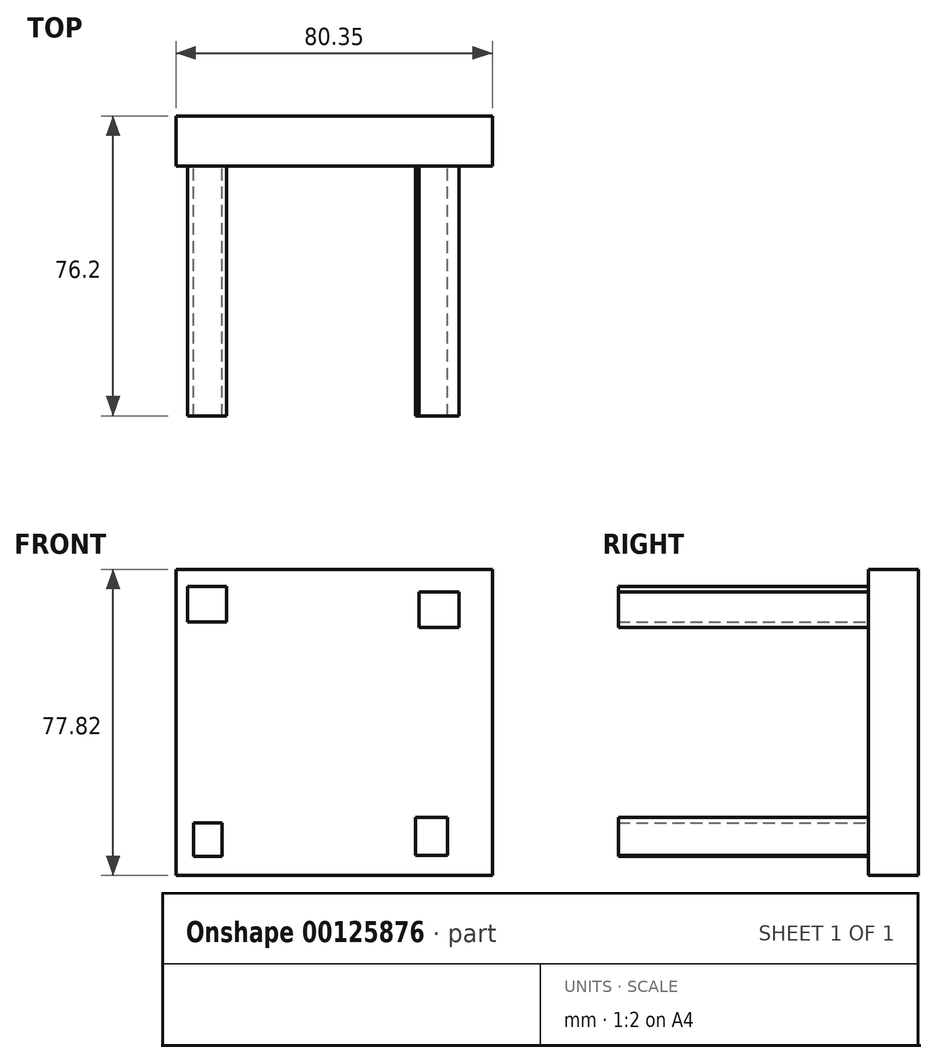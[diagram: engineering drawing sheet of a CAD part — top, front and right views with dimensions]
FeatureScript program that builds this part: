
annotation { "Feature Type Name" : "Feature", "Feature Type Description" : "" }
export const myFeature = defineFeature(function(context is Context, id is Id, definition is map)
    precondition{}
    {
        {
            var Q0;
            Q0=qCreatedBy(makeId("Front.planeOp"),FACE);
            var sketch = newSketch(context, id + "F0", { "sketchPlane" : qUnion([Q0])});
            skLineSegment(sketch, "E0.bottom", {"start": v(-38.21, 36.6) * mm, "end": v(42.14, 36.6) * mm});
            skLineSegment(sketch, "E0.top", {"start": v(-38.21, -41.22) * mm, "end": v(42.14, -41.22) * mm});
            skLineSegment(sketch, "E0.left", {"start": v(-38.21, 36.6) * mm, "end": v(-38.21, -41.22) * mm});
            skLineSegment(sketch, "E0.right", {"start": v(42.14, 36.6) * mm, "end": v(42.14, -41.22) * mm});
            skSolve(sketch);
        }
        {
            var Q0;
            Q0 = qSketchRegion(id + "F0", true);
            extrude(context, id + "F1", {"entities" : qUnion([Q0]), "depth" : 12.7 * mm});
        }
        {
            var Q0;
            Q0=qCreatedBy(makeId("Front.planeOp"),FACE);
            var sketch = newSketch(context, id + "F2", { "sketchPlane" : qUnion([Q0])});
            skLineSegment(sketch, "E1.bottom", {"start": v(-35.33, 32.21) * mm, "end": v(-25.4, 32.21) * mm});
            skLineSegment(sketch, "E1.top", {"start": v(-35.33, 23.2) * mm, "end": v(-25.4, 23.2) * mm});
            skLineSegment(sketch, "E1.left", {"start": v(-35.33, 32.21) * mm, "end": v(-35.33, 23.2) * mm});
            skLineSegment(sketch, "E1.right", {"start": v(-25.4, 32.21) * mm, "end": v(-25.4, 23.2) * mm});
            skSolve(sketch);
        }
        {
            var Q0;
            Q0 = qSketchRegion(id + "F2", true);
            extrude(context, id + "F3", {"entities" : qUnion([Q0]), "operationType" : NewBodyOperationType.ADD, "depth" : 76.2 * mm});
        }
        {
            var Q0;
            Q0=qCreatedBy(makeId("Front.planeOp"),FACE);
            var sketch = newSketch(context, id + "F4", { "sketchPlane" : qUnion([Q0])});
            skLineSegment(sketch, "E2.bottom", {"start": v(23.55, 30.83) * mm, "end": v(33.71, 30.83) * mm});
            skLineSegment(sketch, "E2.top", {"start": v(23.55, 21.82) * mm, "end": v(33.71, 21.82) * mm});
            skLineSegment(sketch, "E2.left", {"start": v(23.55, 30.83) * mm, "end": v(23.55, 21.82) * mm});
            skLineSegment(sketch, "E2.right", {"start": v(33.71, 30.83) * mm, "end": v(33.71, 21.82) * mm});
            skSolve(sketch);
        }
        {
            var Q0;
            Q0 = qSketchRegion(id + "F4", true);
            extrude(context, id + "F5", {"entities" : qUnion([Q0]), "operationType" : NewBodyOperationType.ADD, "depth" : 76.2 * mm});
        }
        {
            var Q0;
            Q0=qCreatedBy(makeId("Front.planeOp"),FACE);
            var sketch = newSketch(context, id + "F6", { "sketchPlane" : qUnion([Q0])});
            skLineSegment(sketch, "E3.bottom", {"start": v(-33.71, -27.82) * mm, "end": v(-26.55, -27.82) * mm});
            skLineSegment(sketch, "E3.top", {"start": v(-33.71, -36.37) * mm, "end": v(-26.55, -36.37) * mm});
            skLineSegment(sketch, "E3.left", {"start": v(-33.71, -27.82) * mm, "end": v(-33.71, -36.37) * mm});
            skLineSegment(sketch, "E3.right", {"start": v(-26.55, -27.82) * mm, "end": v(-26.55, -36.37) * mm});
            skSolve(sketch);
        }
        {
            var Q0;
            Q0 = qSketchRegion(id + "F6", true);
            extrude(context, id + "F7", {"entities" : qUnion([Q0]), "operationType" : NewBodyOperationType.ADD, "depth" : 76.2 * mm});
        }
        {
            var Q0;
            Q0=qCreatedBy(makeId("Front.planeOp"),FACE);
            var sketch = newSketch(context, id + "F8", { "sketchPlane" : qUnion([Q0])});
            skLineSegment(sketch, "E4.bottom", {"start": v(22.63, -26.44) * mm, "end": v(30.71, -26.44) * mm});
            skLineSegment(sketch, "E4.top", {"start": v(22.63, -36.14) * mm, "end": v(30.71, -36.14) * mm});
            skLineSegment(sketch, "E4.left", {"start": v(22.63, -26.44) * mm, "end": v(22.63, -36.14) * mm});
            skLineSegment(sketch, "E4.right", {"start": v(30.71, -26.44) * mm, "end": v(30.71, -36.14) * mm});
            skSolve(sketch);
        }
        {
            var Q0;
            Q0 = qSketchRegion(id + "F8", true);
            extrude(context, id + "F9", {"entities" : qUnion([Q0]), "operationType" : NewBodyOperationType.ADD, "depth" : 76.2 * mm});
        }
    });
